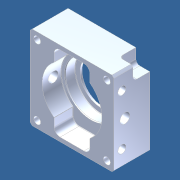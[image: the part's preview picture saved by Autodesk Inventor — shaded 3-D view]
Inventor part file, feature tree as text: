
AUTODESK INVENTOR PART (.ipt)
format: ipt  version: unknown  size: 404,992 bytes
history: native  units: in
note: dims shown in document units (in); Inventor stores cm internally (conversion verified against a paired STEP export)
features: hole x1, imported_body x1
ambient origin geometry x8: Origin, YZ Plane, XZ Plane, XY Plane, X Axis, Y Axis, Z Axis, Center Point
feature tree (2):
  hole  "Hole1"  [1 undecoded]
  imported_body  "Base1"
note: 1 required parameter value undecoded (feature->parameter linkage not recoverable at this tier; creation-order binding heuristic only, values carry confidence <= 0.55)
